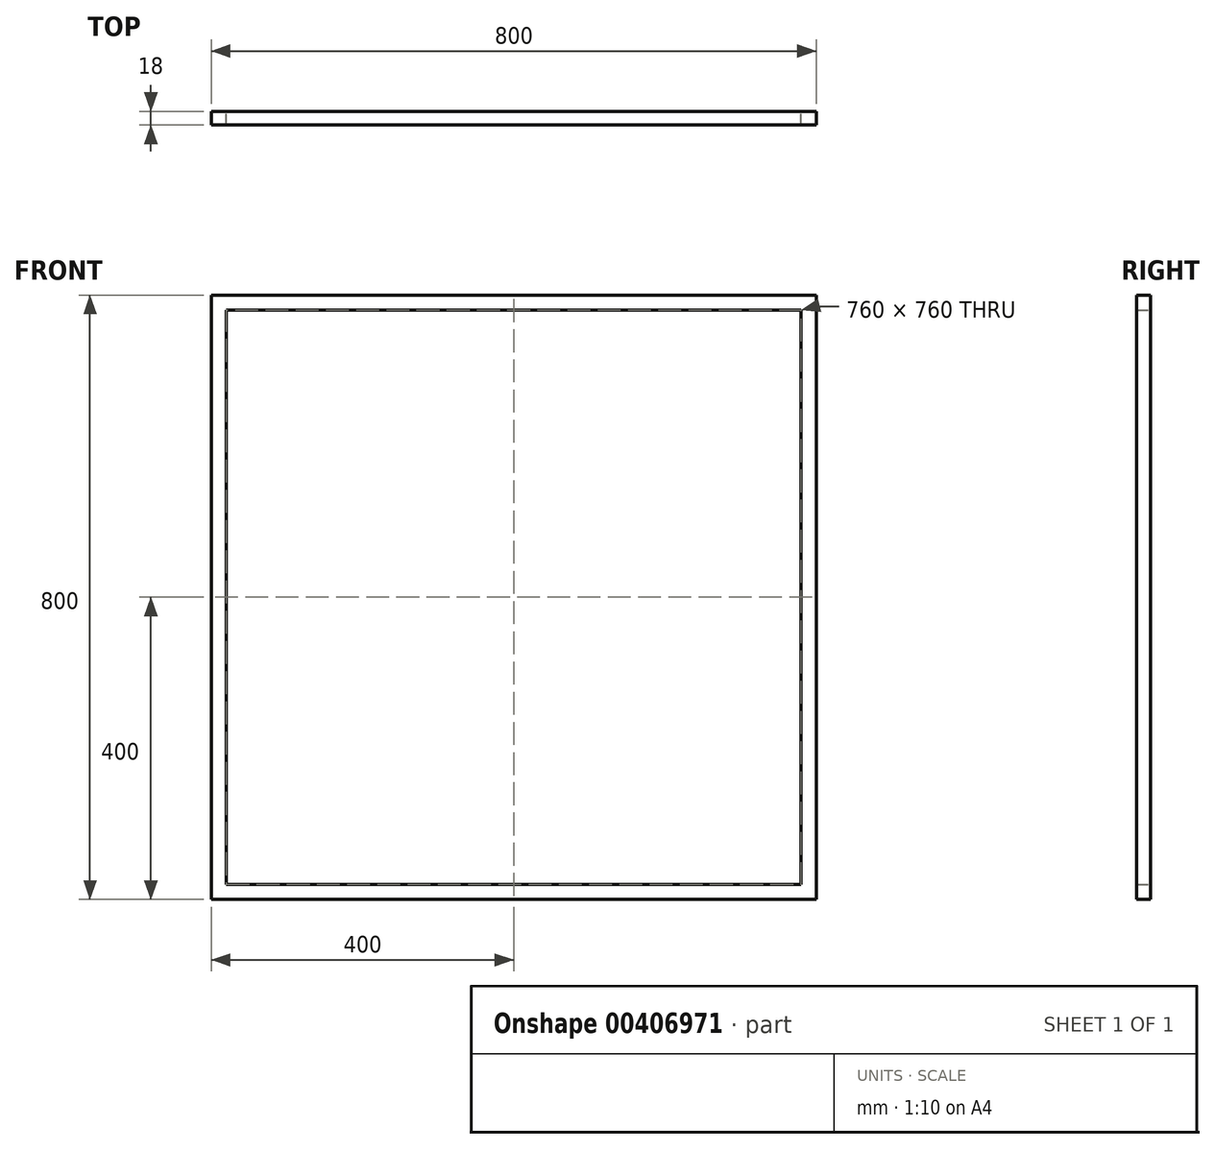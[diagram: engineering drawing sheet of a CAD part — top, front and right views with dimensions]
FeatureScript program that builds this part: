
annotation { "Feature Type Name" : "Feature", "Feature Type Description" : "" }
export const myFeature = defineFeature(function(context is Context, id is Id, definition is map)
    precondition{}
    {
        {
            var Q0;
            Q0=qCreatedBy(makeId("Front.planeOp"),FACE);
            var sketch = newSketch(context, id + "F0", { "sketchPlane" : qUnion([Q0])});
            skLineSegment(sketch, "E0.bottom", {"start": v(400, 400) * mm, "end": v(-400, 400) * mm});
            skLineSegment(sketch, "E0.top", {"start": v(400, -400) * mm, "end": v(-400, -400) * mm});
            skLineSegment(sketch, "E0.left", {"start": v(400, 400) * mm, "end": v(400, -400) * mm});
            skLineSegment(sketch, "E0.right", {"start": v(-400, 400) * mm, "end": v(-400, -400) * mm});
            skPoint(sketch, "E0.middle", {"position": v(0, 0) * mm});
            skLineSegment(sketch, "E1.bottom", {"start": v(380, 380) * mm, "end": v(-380, 380) * mm});
            skLineSegment(sketch, "E1.top", {"start": v(380, -380) * mm, "end": v(-380, -380) * mm});
            skLineSegment(sketch, "E1.left", {"start": v(380, 380) * mm, "end": v(380, -380) * mm});
            skLineSegment(sketch, "E1.right", {"start": v(-380, 380) * mm, "end": v(-380, -380) * mm});
            skSolve(sketch);
        }
        {
            var Q0;
            Q0=makeQuery(id+"F0.imprint","IMPRINT",FACE,{"disambiguationData":[TD([[makeQuery(id+"F0.imprint","IMPRINT",EDGE,{"derivedFrom":sQuery(id+"F0.wireOp",EDGE,"E0.bottom")}),1.0]])]});
            extrude(context, id + "F1", {"entities" : qUnion([Q0]), "depth" : 18 * mm});
        }
    });
